# Revit family: Diffuser-Carnes-SKTA-T_Bar
name_source: partatom
category: Duct Accessories
revit_build: Autodesk Revit Architecture 2012 (Build: 20110309_2315(x64)
units: mm (PartAtom-declared; Revit-internal decimal feet)

## types (34) — shared parameters
Catalog = http://www.carnes.com
Default Elevation = 0"
Description = Square and Rectangular Diffusers
Manufacturer = CARNES COMPANY
Model = SKTA
Product Page URL = http://www.carnes.com
Rapid Induction Vanes = http://www.carnes.com
Round Neck Option = http://www.carnes.com
Specification Sheet = http://www.carnes.com
Subcatagory = Air Distribution
URL = http://www.carnes.com
Unit = Metal - Carnes - Steel Galvanized

## per-type parameters (varying)
| type | Blade Offset | Diffuser Depth B | Diffuser Width A | Plate Depth D | Plate Width C |
| SKTA 6x6 11 | 3/4" | 6" | 6" | 11 3/4" | 11 3/4" |
| SKTA 6x6 47 | 3/4" | 6" | 6" | 47 3/4" | 47 3/4" |
| SKTA 6x9 11 | 3/4" | 9" | 6" | 11 3/4" | 11 3/4" |
| SKTA 6x9 47 | 3/4" | 9" | 6" | 47 3/4" | 47 3/4" |
| SKTA 6x12 11 | 3/4" | 12" | 6" | 23 3/4" | 11 3/4" |
| SKTA 6x12x47 | 3/4" | 12" | 6" | 47 3/4" | 47 3/4" |
| SKTA 6x15x11 | 3/4" | 15" | 6" | 23 3/4" | 11 3/4" |
| SKTA 6x15x47 | 3/4" | 15" | 6" | 47 3/4" | 47 3/4" |
| SKTA 6x18x11 | 3/4" | 18" | 6" | 23 3/4" | 11 3/4" |
| SKTA 6x18x47 | 3/4" | 18" | 6" | 47 3/4" | 47 3/4" |
| SKTA 6x21x11 | 3/4" | 21" | 6" | 23 3/4" | 11 3/4" |
| SKTA 6x21x47 | 3/4" | 21" | 6" | 47 3/4" | 47 3/4" |
| SKTA 9x9x11 | 1 1/2" | 9" | 9" | 11 3/4" | 11 3/4" |
| SKTA 9x9x47 | 1 1/2" | 9" | 9" | 47 3/4" | 47 3/4" |
| SKTA 9x12x11 | 1 1/2" | 12" | 9" | 23 3/4" | 11 3/4" |
| SKTA 9x12x47 | 1 1/2" | 12" | 9" | 47 3/4" | 47 3/4" |
| SKTA 9x15x11 | 1 1/2" | 15" | 9" | 23 3/4" | 11 3/4" |
| SKTA 9x15x47 | 1 1/2" | 15" | 9" | 47 3/4" | 47 3/4" |
| SKTA 9x18x11 | 1 1/2" | 18" | 9" | 23 3/4" | 11 3/4" |
| SKTA 9x18x47 | 1 1/2" | 18" | 9" | 47 3/4" | 47 3/4" |
| SKTA 9x21x11 | 1 1/2" | 21" | 9" | 47 3/4" | 47 3/4" |
| SKTA 9x21x47 | 1 1/2" | 21" | 9" | 47 3/4" | 47 3/4" |
| SKTA 12x12x47 | 1 1/2" | 12" | 12" | 47 3/4" | 47 3/4" |
| SKTA 12x15x47 | 1 1/2" | 15" | 12" | 47 3/4" | 47 3/4" |
| SKTA 12x18x47 | 1 1/2" | 18" | 12" | 47 3/4" | 47 3/4" |
| SKTA 12x21x47 | 1 1/2" | 21" | 12" | 47 3/4" | 47 3/4" |
| SKTA 15x15x47 | 1 1/2" | 15" | 15" | 47 3/4" | 47 3/4" |
| SKTA 15x18x47 | 1 1/2" | 18" | 15" | 47 3/4" | 47 3/4" |
| SKTA 15x21x47 | 1 1/2" | 21" | 15" | 47 3/4" | 47 3/4" |
| SKTA 18x18x47 | 1 1/2" | 18" | 18" | 47 3/4" | 47 3/4" |
| SKTA 18x21x47 | 1 1/2" | 21" | 18" | 47 3/4" | 47 3/4" |
| SKTA 21x21x47 | 1 1/2" | 21" | 21" | 47 3/4" | 47 3/4" |
| SKTA 21x24x47 | 1 1/2" | 24" | 21" | 47 3/4" | 47 3/4" |
| SKTA 24x24x47 | 1 1/2" | 24" | 24" | 47 3/4" | 47 3/4" |

## geometry (parser evidence)
native form markers: Blend x2, Sweep x3
no freeform markers — native parametric forms only
